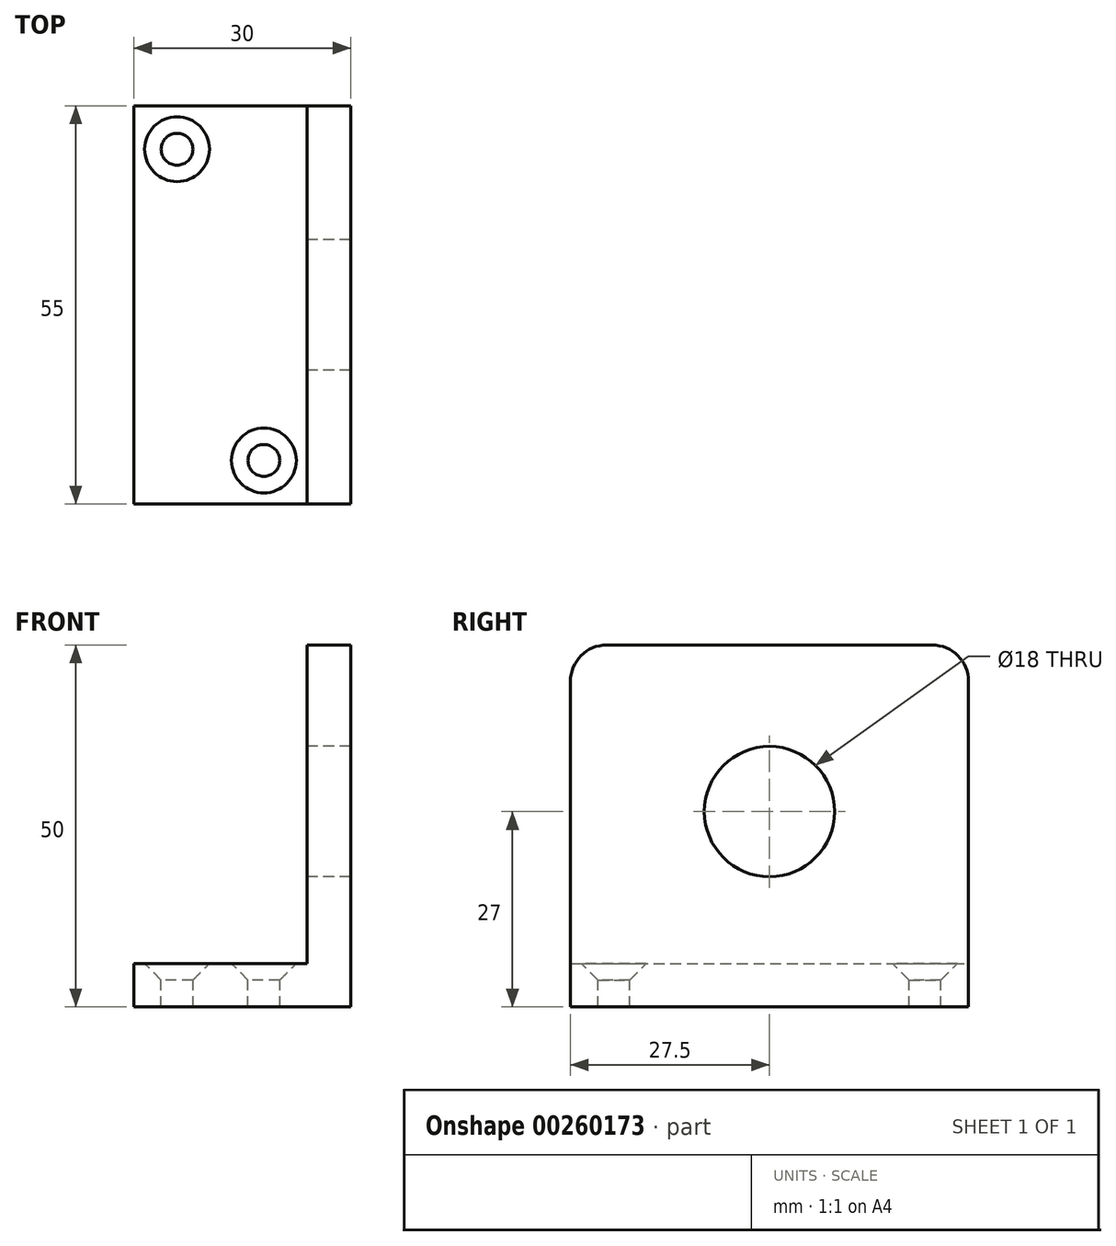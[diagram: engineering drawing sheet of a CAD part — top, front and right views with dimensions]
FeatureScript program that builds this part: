
annotation { "Feature Type Name" : "Feature", "Feature Type Description" : "" }
export const myFeature = defineFeature(function(context is Context, id is Id, definition is map)
    precondition{}
    {
        {
            var Q0;
            Q0=qCreatedBy(makeId("Front.planeOp"),FACE);
            var sketch = newSketch(context, id + "F0", { "sketchPlane" : qUnion([Q0])});
            skLineSegment(sketch, "E0", {"start": v(0, 0) * mm, "end": v(30, 0) * mm});
            skLineSegment(sketch, "E1", {"start": v(30, 0) * mm, "end": v(30, 50) * mm});
            skLineSegment(sketch, "E2", {"start": v(30, 50) * mm, "end": v(24, 50) * mm});
            skLineSegment(sketch, "E3", {"start": v(24, 50) * mm, "end": v(24, 6) * mm});
            skLineSegment(sketch, "E4", {"start": v(24, 6) * mm, "end": v(0, 6) * mm});
            skLineSegment(sketch, "E5", {"start": v(0, 6) * mm, "end": v(0, 0) * mm});
            skSolve(sketch);
        }
        {
            var Q0;
            Q0=makeQuery(id+"F0.imprint","IMPRINT",FACE,{"disambiguationData":[TD([[makeQuery(id+"F0.imprint","IMPRINT",EDGE,{"derivedFrom":sQuery(id+"F0.wireOp",EDGE,"E0")}),1.0]])]});
            extrude(context, id + "F1", {"entities" : qUnion([Q0]), "depth" : 55 * mm});
        }
        {
            var Q0;
            Q0=makeQuery(id+"F1.opExtrude","CAP_EDGE",EDGE,{"disambiguationData":[OSD([sQuery(id+"F0.wireOp",EDGE,"E2")])],"isStart":false});
            var Q1;
            Q1=makeQuery(id+"F1.opExtrude","CAP_EDGE",EDGE,{"disambiguationData":[OSD([sQuery(id+"F0.wireOp",EDGE,"E2")])],"isStart":true});
            fillet(context, id + "F2", {"entities" : qUnion([Q0, Q1]), "radius" : 5 * mm, "tangentPropagation" : true, "allowEdgeOverflow" : false});
        }
        {
            var Q0;
            Q0=makeQuery(id+"F1.opExtrude","SWEPT_FACE",FACE,{"disambiguationData":[OSD([sQuery(id+"F0.wireOp",EDGE,"E3")])]});
            var sketch = newSketch(context, id + "F3", { "sketchPlane" : qUnion([Q0])});
            skCircle(sketch, "E6", {"center": v(27.5, 27) * mm, "radius": 9 * mm});
            skSolve(sketch);
        }
        {
            var Q0;
            Q0=makeQuery(id+"F3.imprint","IMPRINT",FACE,{"disambiguationData":[TD([[makeQuery(id+"F3.imprint","IMPRINT",EDGE,{"derivedFrom":sQuery(id+"F3.wireOp",EDGE,"E6")}),1.0]])]});
            extrude(context, id + "F4", {"entities" : qUnion([Q0]), "operationType" : NewBodyOperationType.REMOVE, "endBound" : BoundingType.THROUGH_ALL, "oppositeDirection" : true, "depth" : 25 * mm});
        }
        {
            var Q0;
            Q0=makeQuery(id+"F1.opExtrude","SWEPT_FACE",FACE,{"disambiguationData":[OSD([sQuery(id+"F0.wireOp",EDGE,"E4")])]});
            var sketch = newSketch(context, id + "F5", { "sketchPlane" : qUnion([Q0])});
            skPoint(sketch, "E7", {"position": v(6, -6) * mm});
            skPoint(sketch, "E8", {"position": v(18, -49) * mm});
            skSolve(sketch);
        }
        {
            var Q0;
            Q0=sQuery(id+"F5.wireOp",VERTEX,"E7");
            var Q1;
            Q1=sQuery(id+"F5.wireOp",VERTEX,"E8");
            var Q2;
            Q2=makeQuery(id+"F1.opExtrude","SWEPT_BODY",BODY,{"disambiguationData":[OSD([sQuery(id+"F0.wireOp",EDGE,"E0"),sQuery(id+"F0.wireOp",EDGE,"E1"),sQuery(id+"F0.wireOp",EDGE,"E2"),sQuery(id+"F0.wireOp",EDGE,"E3"),sQuery(id+"F0.wireOp",EDGE,"E4"),sQuery(id+"F0.wireOp",EDGE,"E5")])]});
            hole(context, id + "F6", {"style" : HoleStyle.C_SINK, "endStyle" : HoleEndStyle.BLIND, "standardTappedOrClearance" : lookupTablePath({ "standard" : "ISO", "fit" : "Normal", "size" : "M4", "type" : "Clearance" }), "standardBlindInLast" : lookupTablePath({ "fit" : "Standard", "standard" : "ISO", "size" : "M4", "type" : "Clearance" }), "holeDiameter" : 4.4 * mm, "cSinkDiameter" : 8.96 * mm, "cSinkAngle" : 90 * degree, "holeDepth" : 18 * mm, "tappedDepth" : 32 * mm, "tapClearance" : 3, "startFromSketch" : true, "locations" : qUnion([Q0, Q1]), "scope" : qUnion([Q2])});
        }
    });
